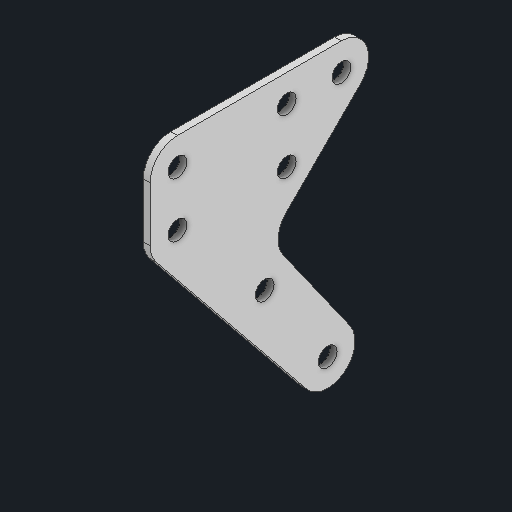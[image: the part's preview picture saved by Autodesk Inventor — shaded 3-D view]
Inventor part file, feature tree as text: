
AUTODESK INVENTOR PART (.ipt)
format: ipt  version: 2025 (Build 290162000, 162)  size: 124,416 bytes
history: native  units: in
note: dims shown in document units (in); Inventor stores cm internally (conversion verified against a paired STEP export)
features: other x3, extrude x1, sketch x1
ambient origin geometry x8: Origin, YZ Plane, XZ Plane, XY Plane, X Axis, Y Axis, Z Axis, Center Point
bodies: Solid1 (feature_tree)
feature tree (5):
  other  "Blocks"
  extrude  "Extrusion1"  Depth=0.0625in
  sketch  "Sketch1"  dims[d0=0.5in d1=0.5in d4=0.25in d5=0.5in d6=0.172in d7=0.0625in d8=0.0in]
  other  "maiin"
  other  "maiin:1"
